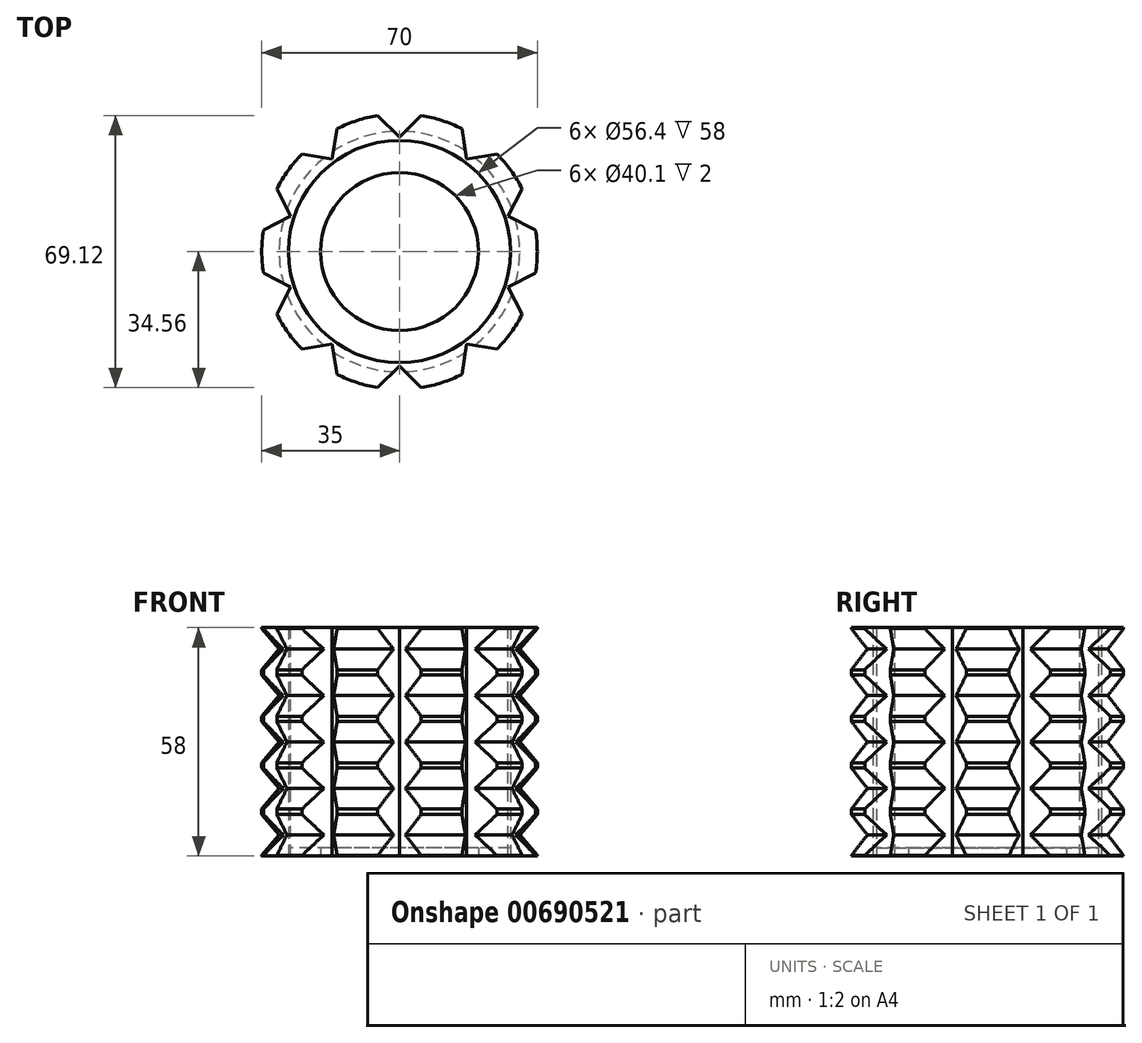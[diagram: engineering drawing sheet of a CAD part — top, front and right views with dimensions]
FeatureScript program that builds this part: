
annotation { "Feature Type Name" : "Feature", "Feature Type Description" : "" }
export const myFeature = defineFeature(function(context is Context, id is Id, definition is map)
    precondition{}
    {
        {
            var Q0;
            Q0=qCreatedBy(makeId("Top.planeOp"),FACE);
            var sketch = newSketch(context, id + "F0", { "sketchPlane" : qUnion([Q0])});
            skCircle(sketch, "E0", {"center": v(0, 0) * mm, "radius": 20.05 * mm});
            skCircle(sketch, "E1", {"center": v(0, 0) * mm, "radius": 28.2 * mm});
            skSolve(sketch);
        }
        {
            var Q0;
            Q0 = qSketchRegion(id + "F0", true);
            extrude(context, id + "F1", {"entities" : qUnion([Q0]), "depth" : 2 * mm, "offsetDistance" : 25 * mm});
        }
        {
            var Q0;
            Q0=makeQuery(id+"F1.opExtrude","CAP_FACE",FACE,{"disambiguationData":[OSD([sQuery(id+"F0.wireOp",EDGE,"E0"),sQuery(id+"F0.wireOp",EDGE,"E1")])],"isStart":true});
            var sketch = newSketch(context, id + "F2", { "sketchPlane" : qUnion([Q0])});
            skCircle(sketch, "E2", {"center": v(0, 0) * mm, "radius": 35 * mm});
            skCircle(sketch, "E3.0", {"center": v(0, 0) * mm, "radius": 28.2 * mm});
            skSolve(sketch);
        }
        {
            var Q0;
            Q0 = qSketchRegion(id + "F2", true);
            extrude(context, id + "F3", {"entities" : qUnion([Q0]), "oppositeDirection" : true, "depth" : 58 * mm, "offsetDistance" : 25 * mm});
        }
        {
            var Q0;
            Q0=qCreatedBy(makeId("Front.planeOp"),FACE);
            var sketch = newSketch(context, id + "F4", { "sketchPlane" : qUnion([Q0])});
            skLineSegment(sketch, "E4", {"start": v(-35.09, 0) * mm, "end": v(-30.56, 5.34) * mm});
            skLineSegment(sketch, "E5", {"start": v(-30.56, 5.34) * mm, "end": v(-35.09, 10.68) * mm});
            skLineSegment(sketch, "E6", {"start": v(-35.09, 0) * mm, "end": v(-35.09, 10.68) * mm});
            skLineSegment(sketch, "E7.0.1.0", {"start": v(-30.56, 17.14) * mm, "end": v(-35.09, 22.48) * mm});
            skLineSegment(sketch, "E7.0.1.1", {"start": v(-35.09, 11.8) * mm, "end": v(-35.09, 22.48) * mm});
            skLineSegment(sketch, "E7.0.1.2", {"start": v(-35.09, 11.8) * mm, "end": v(-30.56, 17.14) * mm});
            skLineSegment(sketch, "E7.0.2.0", {"start": v(-30.56, 28.94) * mm, "end": v(-35.09, 34.28) * mm});
            skLineSegment(sketch, "E7.0.2.1", {"start": v(-35.09, 23.6) * mm, "end": v(-35.09, 34.28) * mm});
            skLineSegment(sketch, "E7.0.2.2", {"start": v(-35.09, 23.6) * mm, "end": v(-30.56, 28.94) * mm});
            skLineSegment(sketch, "E7.0.3.0", {"start": v(-30.56, 40.74) * mm, "end": v(-35.09, 46.08) * mm});
            skLineSegment(sketch, "E7.0.3.1", {"start": v(-35.09, 35.4) * mm, "end": v(-35.09, 46.08) * mm});
            skLineSegment(sketch, "E7.0.3.2", {"start": v(-35.09, 35.4) * mm, "end": v(-30.56, 40.74) * mm});
            skLineSegment(sketch, "E7.0.4.0", {"start": v(-30.56, 52.54) * mm, "end": v(-35.09, 57.88) * mm});
            skLineSegment(sketch, "E7.0.4.1", {"start": v(-35.09, 47.2) * mm, "end": v(-35.09, 57.88) * mm});
            skLineSegment(sketch, "E7.0.4.2", {"start": v(-35.09, 47.2) * mm, "end": v(-30.56, 52.54) * mm});
            skLineSegment(sketch, "E7.direction1", {"start": v(-30.56, 5.34) * mm, "end": v(-55.56, 5.34) * mm, "construction": true});
            skLineSegment(sketch, "E7.direction2", {"start": v(-30.56, 5.34) * mm, "end": v(-30.56, 17.14) * mm, "construction": true});
            skLineSegment(sketch, "E8", {"start": v(0, 0) * mm, "end": v(0, 62.43) * mm});
            skSolve(sketch);
        }
        {
            var Q0;
            Q0 = qSketchRegion(id + "F4", true);
            var Q1;
            Q1=sQuery(id+"F4.wireOp",EDGE,"E8");
            revolve(context, id + "F5", {"operationType" : NewBodyOperationType.REMOVE, "entities" : qUnion([Q0]), "axis" : qUnion([Q1]), "revolveType" : RevolveType.FULL, "oppositeDirection" : true});
        }
        {
            var Q0;
            Q0=makeQuery(id+"F3.opExtrude","CAP_FACE",FACE,{"disambiguationData":[OSD([sQuery(id+"F2.wireOp",EDGE,"E2"),sQuery(id+"F2.wireOp",EDGE,"E3.0")])],"isStart":false});
            var sketch = newSketch(context, id + "F6", { "sketchPlane" : qUnion([Q0])});
            skLineSegment(sketch, "E9", {"start": v(0, 29.04) * mm, "end": v(10.9, 39.93) * mm});
            skLineSegment(sketch, "E10", {"start": v(0, 39.5) * mm, "end": v(0, 29.04) * mm});
            skLineSegment(sketch, "E11", {"start": v(10.9, 39.93) * mm, "end": v(0, 39.5) * mm});
            skLineSegment(sketch, "E12.MirrorCS", {"start": v(-10.9, 39.93) * mm, "end": v(0, 39.5) * mm});
            skLineSegment(sketch, "E13.MirrorCS", {"start": v(0, 29.04) * mm, "end": v(-10.9, 39.93) * mm});
            skLineSegment(sketch, "E14.1.0", {"start": v(-17.07, 23.5) * mm, "end": v(-32.28, 25.9) * mm});
            skLineSegment(sketch, "E14.1.1", {"start": v(-32.28, 25.9) * mm, "end": v(-23.22, 31.95) * mm});
            skLineSegment(sketch, "E14.1.2", {"start": v(-14.66, 38.7) * mm, "end": v(-23.22, 31.95) * mm});
            skLineSegment(sketch, "E14.1.3", {"start": v(-23.22, 31.95) * mm, "end": v(-17.07, 23.5) * mm});
            skLineSegment(sketch, "E14.1.4", {"start": v(-17.07, 23.5) * mm, "end": v(-14.66, 38.7) * mm});
            skLineSegment(sketch, "E14.2.0", {"start": v(-27.62, 8.97) * mm, "end": v(-41.34, 1.98) * mm});
            skLineSegment(sketch, "E14.2.1", {"start": v(-41.34, 1.98) * mm, "end": v(-37.56, 12.2) * mm});
            skLineSegment(sketch, "E14.2.2", {"start": v(-34.6, 22.7) * mm, "end": v(-37.56, 12.2) * mm});
            skLineSegment(sketch, "E14.2.3", {"start": v(-37.56, 12.2) * mm, "end": v(-27.62, 8.97) * mm});
            skLineSegment(sketch, "E14.2.4", {"start": v(-27.62, 8.97) * mm, "end": v(-34.6, 22.7) * mm});
            skLineSegment(sketch, "E14.3.0", {"start": v(-27.62, -8.97) * mm, "end": v(-34.6, -22.7) * mm});
            skLineSegment(sketch, "E14.3.1", {"start": v(-34.6, -22.7) * mm, "end": v(-37.56, -12.2) * mm});
            skLineSegment(sketch, "E14.3.2", {"start": v(-41.34, -1.98) * mm, "end": v(-37.56, -12.2) * mm});
            skLineSegment(sketch, "E14.3.3", {"start": v(-37.56, -12.2) * mm, "end": v(-27.62, -8.97) * mm});
            skLineSegment(sketch, "E14.3.4", {"start": v(-27.62, -8.97) * mm, "end": v(-41.34, -1.98) * mm});
            skLineSegment(sketch, "E14.4.0", {"start": v(-17.07, -23.5) * mm, "end": v(-14.66, -38.7) * mm});
            skLineSegment(sketch, "E14.4.1", {"start": v(-14.66, -38.7) * mm, "end": v(-23.22, -31.95) * mm});
            skLineSegment(sketch, "E14.4.2", {"start": v(-32.28, -25.9) * mm, "end": v(-23.22, -31.95) * mm});
            skLineSegment(sketch, "E14.4.3", {"start": v(-23.22, -31.95) * mm, "end": v(-17.07, -23.5) * mm});
            skLineSegment(sketch, "E14.4.4", {"start": v(-17.07, -23.5) * mm, "end": v(-32.28, -25.9) * mm});
            skLineSegment(sketch, "E14.5.0", {"start": v(0, -29.04) * mm, "end": v(10.9, -39.93) * mm});
            skLineSegment(sketch, "E14.5.1", {"start": v(10.9, -39.93) * mm, "end": v(0, -39.5) * mm});
            skLineSegment(sketch, "E14.5.2", {"start": v(-10.9, -39.93) * mm, "end": v(0, -39.5) * mm});
            skLineSegment(sketch, "E14.5.3", {"start": v(0, -39.5) * mm, "end": v(0, -29.04) * mm});
            skLineSegment(sketch, "E14.5.4", {"start": v(0, -29.04) * mm, "end": v(-10.9, -39.93) * mm});
            skLineSegment(sketch, "E14.6.0", {"start": v(17.07, -23.5) * mm, "end": v(32.28, -25.9) * mm});
            skLineSegment(sketch, "E14.6.1", {"start": v(32.28, -25.9) * mm, "end": v(23.22, -31.95) * mm});
            skLineSegment(sketch, "E14.6.2", {"start": v(14.66, -38.7) * mm, "end": v(23.22, -31.95) * mm});
            skLineSegment(sketch, "E14.6.3", {"start": v(23.22, -31.95) * mm, "end": v(17.07, -23.5) * mm});
            skLineSegment(sketch, "E14.6.4", {"start": v(17.07, -23.5) * mm, "end": v(14.66, -38.7) * mm});
            skLineSegment(sketch, "E14.7.0", {"start": v(27.62, -8.97) * mm, "end": v(41.34, -1.98) * mm});
            skLineSegment(sketch, "E14.7.1", {"start": v(41.34, -1.98) * mm, "end": v(37.56, -12.2) * mm});
            skLineSegment(sketch, "E14.7.2", {"start": v(34.6, -22.7) * mm, "end": v(37.56, -12.2) * mm});
            skLineSegment(sketch, "E14.7.3", {"start": v(37.56, -12.2) * mm, "end": v(27.62, -8.97) * mm});
            skLineSegment(sketch, "E14.7.4", {"start": v(27.62, -8.97) * mm, "end": v(34.6, -22.7) * mm});
            skLineSegment(sketch, "E14.8.0", {"start": v(27.62, 8.97) * mm, "end": v(34.6, 22.7) * mm});
            skLineSegment(sketch, "E14.8.1", {"start": v(34.6, 22.7) * mm, "end": v(37.56, 12.2) * mm});
            skLineSegment(sketch, "E14.8.2", {"start": v(41.34, 1.98) * mm, "end": v(37.56, 12.2) * mm});
            skLineSegment(sketch, "E14.8.3", {"start": v(37.56, 12.2) * mm, "end": v(27.62, 8.97) * mm});
            skLineSegment(sketch, "E14.8.4", {"start": v(27.62, 8.97) * mm, "end": v(41.34, 1.98) * mm});
            skLineSegment(sketch, "E14.9.0", {"start": v(17.07, 23.5) * mm, "end": v(14.66, 38.7) * mm});
            skLineSegment(sketch, "E14.9.1", {"start": v(14.66, 38.7) * mm, "end": v(23.22, 31.95) * mm});
            skLineSegment(sketch, "E14.9.2", {"start": v(32.28, 25.9) * mm, "end": v(23.22, 31.95) * mm});
            skLineSegment(sketch, "E14.9.3", {"start": v(23.22, 31.95) * mm, "end": v(17.07, 23.5) * mm});
            skLineSegment(sketch, "E14.9.4", {"start": v(17.07, 23.5) * mm, "end": v(32.28, 25.9) * mm});
            skPoint(sketch, "E14.center", {"position": v(0, 0) * mm});
            skSolve(sketch);
        }
        {
            var Q0;
            Q0 = qSketchRegion(id + "F6", true);
            extrude(context, id + "F7", {"entities" : qUnion([Q0]), "operationType" : NewBodyOperationType.REMOVE, "endBound" : BoundingType.THROUGH_ALL, "oppositeDirection" : true, "depth" : 25 * mm, "offsetDistance" : 25 * mm});
        }
    });
